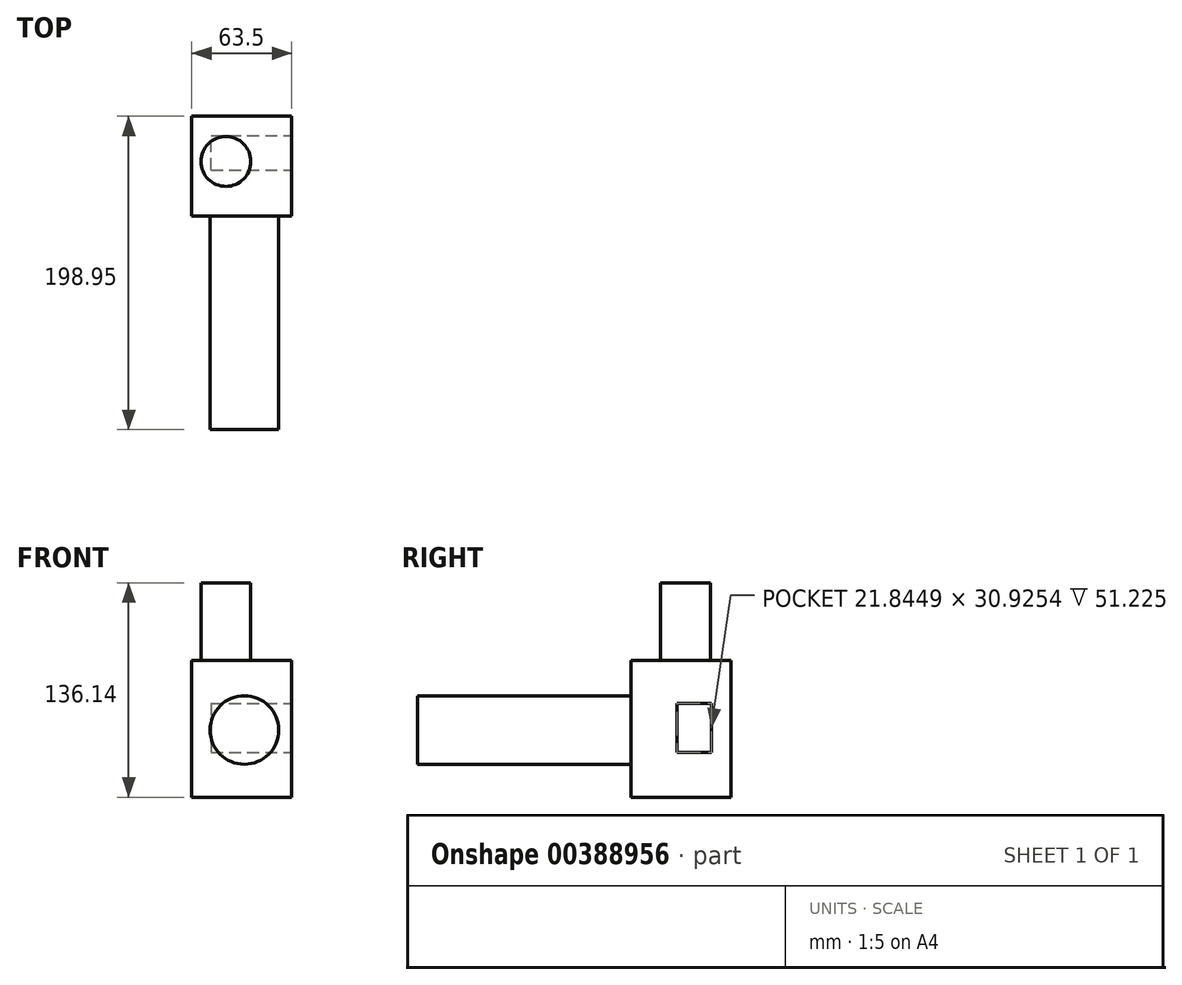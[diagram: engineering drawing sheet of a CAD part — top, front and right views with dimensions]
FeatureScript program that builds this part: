
annotation { "Feature Type Name" : "Feature", "Feature Type Description" : "" }
export const myFeature = defineFeature(function(context is Context, id is Id, definition is map)
    precondition{}
    {
        {
            var Q0;
            Q0=qCreatedBy(makeId("Front.planeOp"),FACE);
            var sketch = newSketch(context, id + "F0", { "sketchPlane" : qUnion([Q0])});
            skLineSegment(sketch, "E0.bottom", {"start": v(0, 0) * mm, "end": v(63.5, 0) * mm});
            skLineSegment(sketch, "E0.top", {"start": v(0, 86.95) * mm, "end": v(63.5, 86.95) * mm});
            skLineSegment(sketch, "E0.left", {"start": v(0, 0) * mm, "end": v(0, 86.95) * mm});
            skLineSegment(sketch, "E0.right", {"start": v(63.5, 0) * mm, "end": v(63.5, 86.95) * mm});
            skSolve(sketch);
        }
        {
            var Q0;
            Q0=makeQuery(id+"F0.imprint","IMPRINT",FACE,{"disambiguationData":[TD([[makeQuery(id+"F0.imprint","IMPRINT",EDGE,{"derivedFrom":sQuery(id+"F0.wireOp",EDGE,"E0.bottom")}),1.0]])]});
            extrude(context, id + "F1", {"entities" : qUnion([Q0]), "depth" : 63.5 * mm});
        }
        {
            var Q0;
            Q0=makeQuery(id+"F1.opExtrude","SWEPT_FACE",FACE,{"disambiguationData":[OSD([sQuery(id+"F0.wireOp",EDGE,"E0.top")])]});
            var sketch = newSketch(context, id + "F2", { "sketchPlane" : qUnion([Q0])});
            skCircle(sketch, "E1", {"center": v(21.68, -28.75) * mm, "radius": 15.84 * mm});
            skSolve(sketch);
        }
        {
            var Q0;
            Q0 = qSketchRegion(id + "F2", true);
            extrude(context, id + "F3", {"entities" : qUnion([Q0]), "operationType" : NewBodyOperationType.ADD, "depth" : 49.2 * mm});
        }
        {
            var Q0;
            Q0=makeQuery(id+"F1.opExtrude","SWEPT_FACE",FACE,{"disambiguationData":[OSD([sQuery(id+"F0.wireOp",EDGE,"E0.right")])]});
            var sketch = newSketch(context, id + "F4", { "sketchPlane" : qUnion([Q0])});
            skLineSegment(sketch, "E2.bottom", {"start": v(-34.19, 59.48) * mm, "end": v(-12.34, 59.48) * mm});
            skLineSegment(sketch, "E2.top", {"start": v(-34.19, 28.55) * mm, "end": v(-12.34, 28.55) * mm});
            skLineSegment(sketch, "E2.left", {"start": v(-34.19, 59.48) * mm, "end": v(-34.19, 28.55) * mm});
            skLineSegment(sketch, "E2.right", {"start": v(-12.34, 59.48) * mm, "end": v(-12.34, 28.55) * mm});
            skPoint(sketch, "E2.middle", {"position": v(-23.26, 44.01) * mm});
            skSolve(sketch);
        }
        {
            var Q0;
            Q0 = qSketchRegion(id + "F4", true);
            var Q1;
            Q1=makeQuery(id+"F4.imprint","IMPRINT",FACE,{"disambiguationData":[TD([[makeQuery(id+"F4.imprint","IMPRINT",EDGE,{"derivedFrom":sQuery(id+"F4.wireOp",EDGE,"E2.bottom")}),-1.0]])]});
            extrude(context, id + "F5", {"entities" : qUnion([Q0, Q1]), "operationType" : NewBodyOperationType.REMOVE, "oppositeDirection" : true, "depth" : 51.23 * mm});
        }
        {
            var Q0;
            Q0=makeQuery(id+"F1.opExtrude","CAP_FACE",FACE,{"disambiguationData":[OSD([sQuery(id+"F0.wireOp",EDGE,"E0.bottom"),sQuery(id+"F0.wireOp",EDGE,"E0.top"),sQuery(id+"F0.wireOp",EDGE,"E0.left"),sQuery(id+"F0.wireOp",EDGE,"E0.right")])],"isStart":false});
            var sketch = newSketch(context, id + "F6", { "sketchPlane" : qUnion([Q0])});
            skCircle(sketch, "E3", {"center": v(33.45, 42.7) * mm, "radius": 21.77 * mm});
            skSolve(sketch);
        }
        {
            var Q0;
            Q0 = qSketchRegion(id + "F6", true);
            extrude(context, id + "F7", {"entities" : qUnion([Q0]), "operationType" : NewBodyOperationType.ADD, "depth" : 135.45 * mm, "offsetDistance" : 25.4 * mm});
        }
    });
